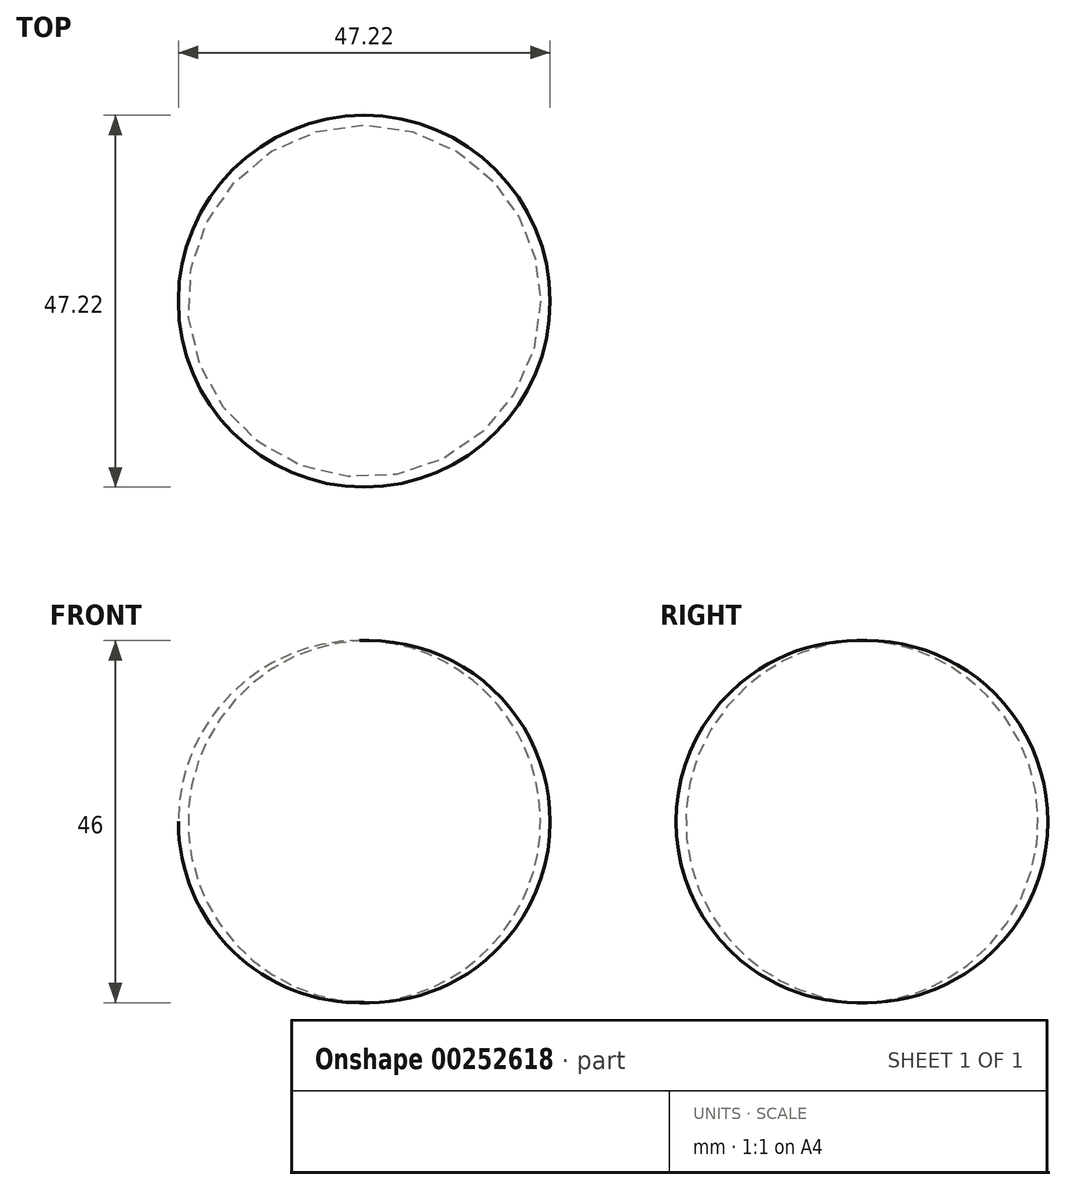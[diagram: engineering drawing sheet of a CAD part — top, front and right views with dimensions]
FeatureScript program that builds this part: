
annotation { "Feature Type Name" : "Feature", "Feature Type Description" : "" }
export const myFeature = defineFeature(function(context is Context, id is Id, definition is map)
    precondition{}
    {
        {
            var Q0;
            Q0=qCreatedBy(makeId("Front.planeOp"),FACE);
            var sketch = newSketch(context, id + "F0", { "sketchPlane" : qUnion([Q0])});
            skLineSegment(sketch, "E0", {"start": v(0, 0) * mm, "end": v(0, 45.98) * mm});
            skArc(sketch, "E1", {"start": v(0, 0) * mm, "mid": v(22.39, 23) * mm, "end": v(0, 45.98) * mm});
            skSolve(sketch);
        }
        {
            var Q0;
            Q0=makeQuery(id+"F0.imprint","IMPRINT",FACE,{"disambiguationData":[TD([[makeQuery(id+"F0.imprint","IMPRINT",EDGE,{"derivedFrom":sQuery(id+"F0.wireOp",EDGE,"E0")}),-1.0]])]});
            var Q1;
            Q1=sQuery(id+"F0.wireOp",EDGE,"E0");
            revolve(context, id + "F1", {"entities" : qUnion([Q0]), "axis" : qUnion([Q1]), "revolveType" : RevolveType.FULL});
        }
    });
